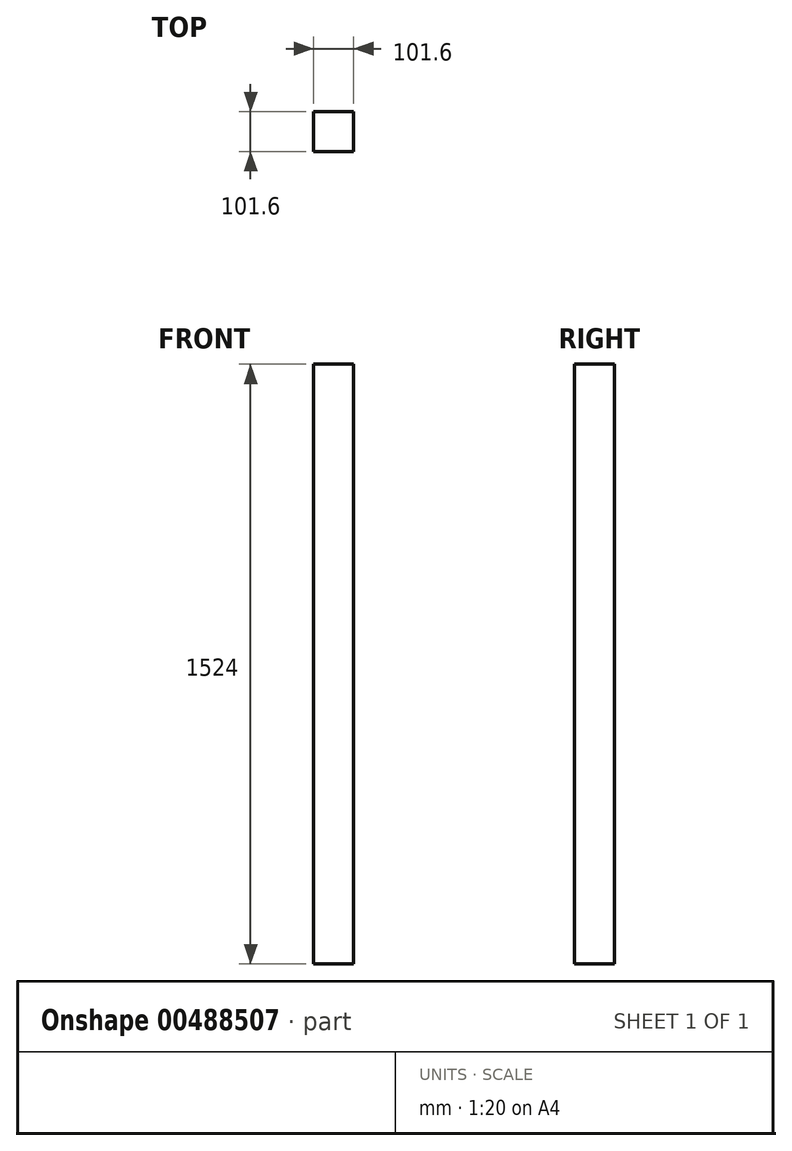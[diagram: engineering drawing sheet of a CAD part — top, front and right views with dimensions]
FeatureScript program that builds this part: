
annotation { "Feature Type Name" : "Feature", "Feature Type Description" : "" }
export const myFeature = defineFeature(function(context is Context, id is Id, definition is map)
    precondition{}
    {
        {
            var Q0;
            Q0=qCreatedBy(makeId("Top.planeOp"),FACE);
            var sketch = newSketch(context, id + "F0", { "sketchPlane" : qUnion([Q0])});
            skLineSegment(sketch, "E0.bottom", {"start": v(-63.37, 50.8) * mm, "end": v(38.23, 50.8) * mm});
            skLineSegment(sketch, "E0.top", {"start": v(-63.37, -50.8) * mm, "end": v(38.23, -50.8) * mm});
            skLineSegment(sketch, "E0.left", {"start": v(-63.37, 50.8) * mm, "end": v(-63.37, -50.8) * mm});
            skLineSegment(sketch, "E0.right", {"start": v(38.23, 50.8) * mm, "end": v(38.23, -50.8) * mm});
            skPoint(sketch, "E0.middle", {"position": v(-12.57, 0) * mm});
            skSolve(sketch);
        }
        {
            var Q0;
            Q0 = qSketchRegion(id + "F0", true);
            extrude(context, id + "F1", {"entities" : qUnion([Q0]), "depth" : 1524 * mm, "offsetDistance" : 25.4 * mm});
        }
    });
